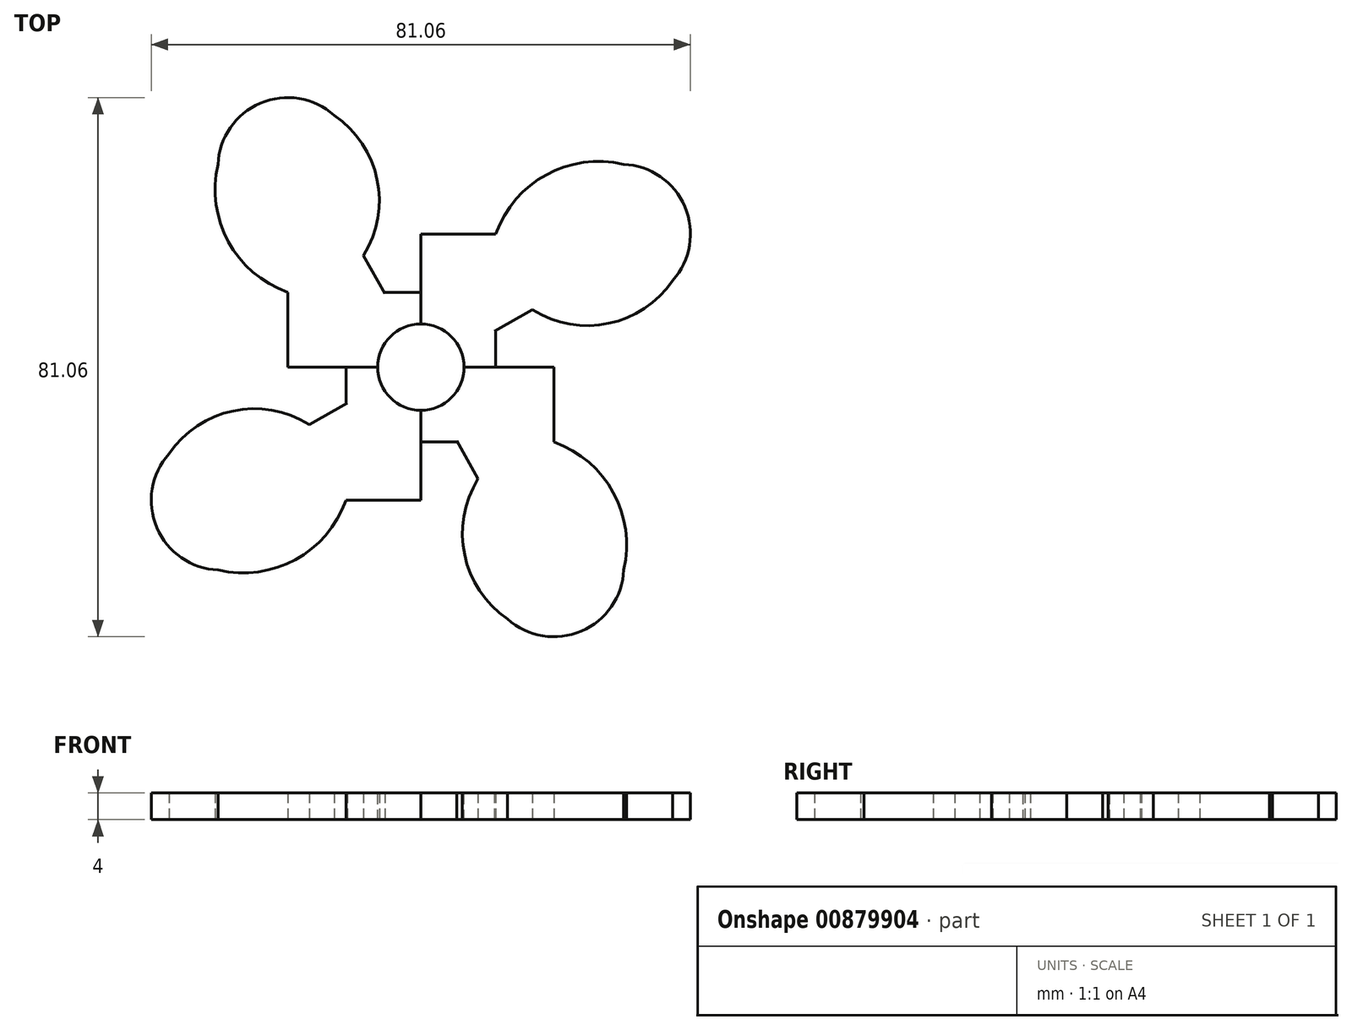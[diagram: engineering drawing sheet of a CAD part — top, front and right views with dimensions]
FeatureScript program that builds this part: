
annotation { "Feature Type Name" : "Feature", "Feature Type Description" : "" }
export const myFeature = defineFeature(function(context is Context, id is Id, definition is map)
    precondition{}
    {
        {
            var Q0;
            Q0=qCreatedBy(makeId("Top.planeOp"),FACE);
            var sketch = newSketch(context, id + "F0", { "sketchPlane" : qUnion([Q0])});
            skLineSegment(sketch, "E0", {"start": v(0, 0) * mm, "end": v(0, 11.26) * mm});
            skLineSegment(sketch, "E1", {"start": v(-5.42, 11.05) * mm, "end": v(-5.42, 11.26) * mm});
            skLineSegment(sketch, "E2", {"start": v(-5.42, 11.05) * mm, "end": v(-8.6, 16.79) * mm});
            skLineSegment(sketch, "E3", {"start": v(-20.02, 11.26) * mm, "end": v(-20.02, 0) * mm});
            skLineSegment(sketch, "E4", {"start": v(-20.02, 0) * mm, "end": v(-11.39, 0) * mm});
            skLineSegment(sketch, "E5", {"start": v(-11.39, 0) * mm, "end": v(0, 0) * mm});
            skLineSegment(sketch, "E6", {"start": v(-5.42, 11.26) * mm, "end": v(0, 11.26) * mm});
            skArc(sketch, "E7", {"start": v(-13.04, 37.86) * mm, "mid": v(-24.11, 39.7) * mm, "end": v(-30.5, 30.47) * mm});
            skArc(sketch, "E8", {"start": v(-8.6, 16.79) * mm, "mid": v(-6.58, 28.22) * mm, "end": v(-13.04, 37.86) * mm});
            skArc(sketch, "E9", {"start": v(-30.5, 30.47) * mm, "mid": v(-28.93, 18.87) * mm, "end": v(-20.02, 11.26) * mm});
            skSolve(sketch);
        }
        {
            var Q0;
            Q0=makeQuery(id+"F0.imprint","IMPRINT",FACE,{"disambiguationData":[TD([[makeQuery(id+"F0.imprint","IMPRINT",EDGE,{"derivedFrom":sQuery(id+"F0.wireOp",EDGE,"E0")}),1.0]])]});
            extrude(context, id + "F1", {"entities" : qUnion([Q0]), "depth" : 4 * mm, "offsetDistance" : 25.4 * mm});
        }
        {
            var Q0;
            Q0=makeQuery(id+"F1.opExtrude","SWEPT_BODY",BODY,{"disambiguationData":[OSD([sQuery(id+"F0.wireOp",EDGE,"E0"),sQuery(id+"F0.wireOp",EDGE,"E1"),sQuery(id+"F0.wireOp",EDGE,"E2"),sQuery(id+"F0.wireOp",EDGE,"ZGwq7lXg-5srX-Ardr-xUZ1-8qm0G1NpKezb"),sQuery(id+"F0.wireOp",EDGE,"cVFeM16D-G9Hr-XGrF-C8Im-RVasLDUvLLpn"),sQuery(id+"F0.wireOp",EDGE,"jWdfa10f-Hr8F-1nc4-8Op0-KhSbMkV0IYzQ"),sQuery(id+"F0.wireOp",EDGE,"ymqsZH4X-EgJ6-xNvV-z14y-7NphwuX3fTVF"),sQuery(id+"F0.wireOp",EDGE,"E3"),sQuery(id+"F0.wireOp",EDGE,"E4"),sQuery(id+"F0.wireOp",EDGE,"E5"),sQuery(id+"F0.wireOp",EDGE,"E6")])]});
            var Q1;
            Q1=makeQuery(id+"F1.opExtrude","SWEPT_EDGE",EDGE,{"disambiguationData":[OSD([sQuery(id+"F0.wireOp",EDGE,"E0"),sQuery(id+"F0.wireOp",EDGE,"E5")])]});
            circularPattern(context, id + "F2", {"entities" : qUnion([Q0]), "axis" : qUnion([Q1]), "angle" : 360 * degree, "instanceCount" : 4, "equalSpace" : true});
        }
        {
            var Q0;
            Q0=makeQuery(id+"F1.opExtrude","CAP_FACE",FACE,{"disambiguationData":[OSD([sQuery(id+"F0.wireOp",EDGE,"E0"),sQuery(id+"F0.wireOp",EDGE,"E1"),sQuery(id+"F0.wireOp",EDGE,"E2"),sQuery(id+"F0.wireOp",EDGE,"ZGwq7lXg-5srX-Ardr-xUZ1-8qm0G1NpKezb"),sQuery(id+"F0.wireOp",EDGE,"cVFeM16D-G9Hr-XGrF-C8Im-RVasLDUvLLpn"),sQuery(id+"F0.wireOp",EDGE,"jWdfa10f-Hr8F-1nc4-8Op0-KhSbMkV0IYzQ"),sQuery(id+"F0.wireOp",EDGE,"ymqsZH4X-EgJ6-xNvV-z14y-7NphwuX3fTVF"),sQuery(id+"F0.wireOp",EDGE,"E3"),sQuery(id+"F0.wireOp",EDGE,"E4"),sQuery(id+"F0.wireOp",EDGE,"E5"),sQuery(id+"F0.wireOp",EDGE,"E6")])],"isStart":false});
            var sketch = newSketch(context, id + "F3", { "sketchPlane" : qUnion([Q0])});
            skCircle(sketch, "E10", {"center": v(0, 0) * mm, "radius": 6.5 * mm});
            skSolve(sketch);
        }
        {
            var Q0;
            {var subQ0=sQuery(id+"F3.wireOp",EDGE,"E10");var subQ1=makeQuery(id+"F1.opExtrude","CAP_EDGE",EDGE,{"disambiguationData":[OSD([sQuery(id+"F0.wireOp",EDGE,"E0")])],"isStart":false});var subQ2=makeQuery(id+"F3.imprint","INTERSECT",VERTEX,{"derivedFrom":[subQ1,subQ0]});Q0=makeQuery(id+"F3.imprint","IMPRINT",FACE,{"disambiguationData":[TD([[makeQuery(id+"F3.imprint","IMPRINT",EDGE,{"disambiguationData":[TD([[subQ2,-1.0]])],"derivedFrom":subQ0}),1.0]])]});}
            var Q1;
            {var subQ0=sQuery(id+"F3.wireOp",EDGE,"E10");var subQ1=makeQuery(id+"F1.opExtrude","CAP_EDGE",EDGE,{"disambiguationData":[OSD([sQuery(id+"F0.wireOp",EDGE,"E0")])],"isStart":false});var subQ2=makeQuery(id+"F3.imprint","INTERSECT",VERTEX,{"derivedFrom":[subQ1,subQ0]});Q1=makeQuery(id+"F3.imprint","IMPRINT",FACE,{"disambiguationData":[TD([[makeQuery(id+"F3.imprint","IMPRINT",EDGE,{"disambiguationData":[TD([[subQ2,1.0]])],"derivedFrom":subQ0}),1.0]])]});}
            extrude(context, id + "F4", {"entities" : qUnion([Q0, Q1]), "operationType" : NewBodyOperationType.REMOVE, "oppositeDirection" : true, "depth" : 5 * mm, "offsetDistance" : 25.4 * mm});
        }
    });
